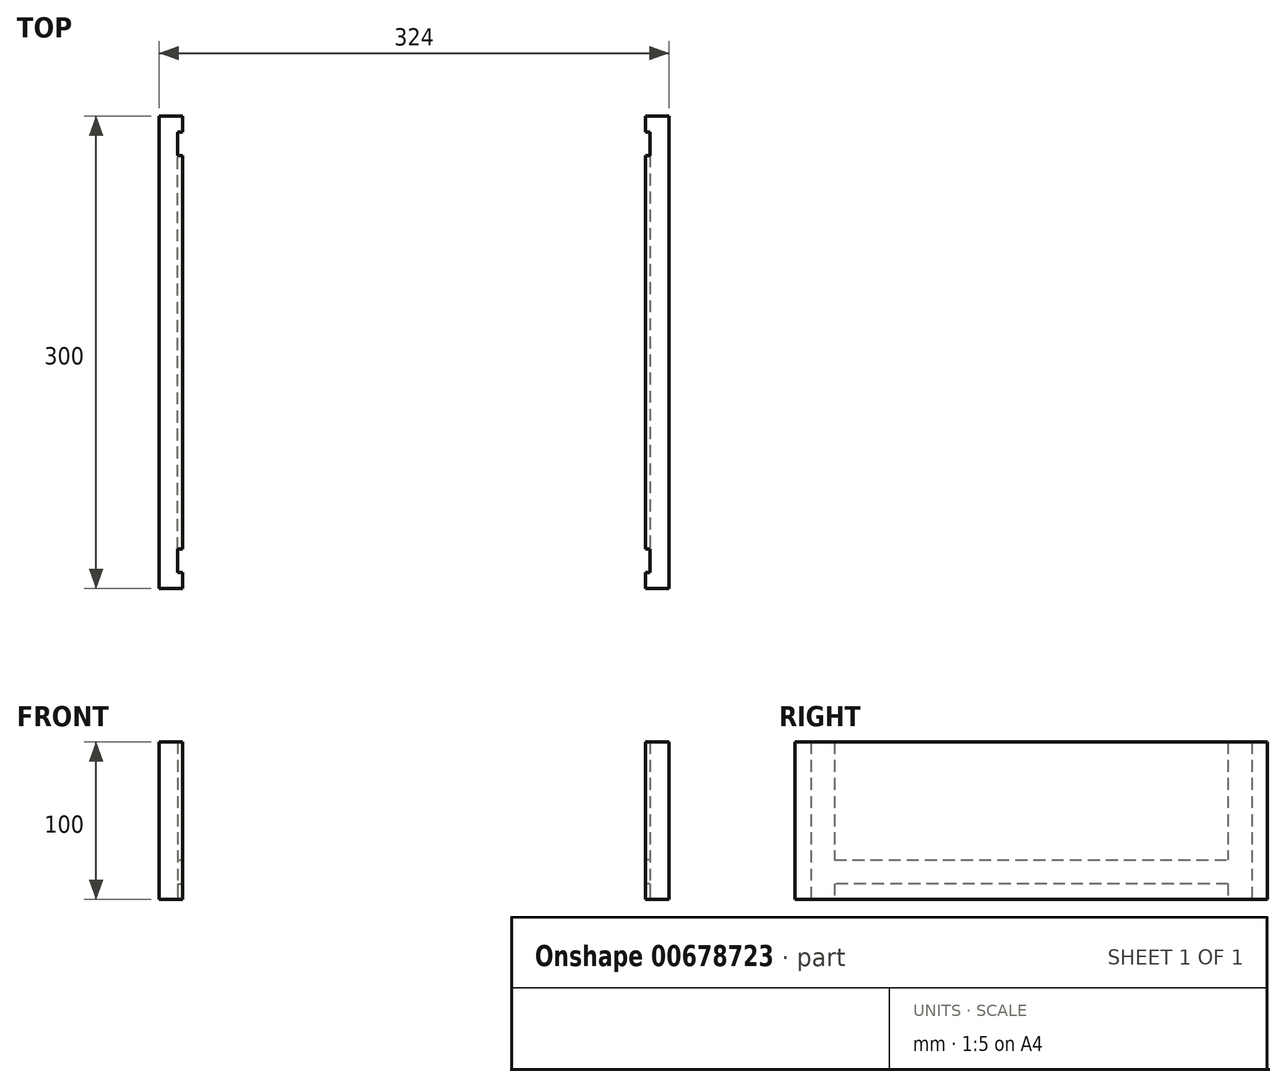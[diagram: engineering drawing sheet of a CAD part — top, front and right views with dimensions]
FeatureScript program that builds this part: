
annotation { "Feature Type Name" : "Feature", "Feature Type Description" : "" }
export const myFeature = defineFeature(function(context is Context, id is Id, definition is map)
    precondition{}
    {
        {
            var Q0;
            Q0=qCreatedBy(makeId("Top.planeOp"),FACE);
            var sketch = newSketch(context, id + "F0", { "sketchPlane" : qUnion([Q0])});
            skLineSegment(sketch, "E0", {"start": v(-162, 0) * mm, "end": v(-147, 0) * mm});
            skLineSegment(sketch, "E1", {"start": v(-147, 0) * mm, "end": v(-147, 10) * mm});
            skLineSegment(sketch, "E2", {"start": v(-147, 10) * mm, "end": v(-150, 10) * mm});
            skLineSegment(sketch, "E3", {"start": v(-150, 10) * mm, "end": v(-150, 25) * mm});
            skLineSegment(sketch, "E4", {"start": v(-150, 25) * mm, "end": v(-147, 25) * mm});
            skLineSegment(sketch, "E5", {"start": v(-147, 25) * mm, "end": v(-147, 275) * mm});
            skLineSegment(sketch, "E6", {"start": v(-147, 275) * mm, "end": v(-150, 275) * mm});
            skLineSegment(sketch, "E7", {"start": v(-150, 275) * mm, "end": v(-150, 290) * mm});
            skLineSegment(sketch, "E8", {"start": v(-150, 290) * mm, "end": v(-147, 290) * mm});
            skLineSegment(sketch, "E9", {"start": v(-147, 290) * mm, "end": v(-147, 300) * mm});
            skLineSegment(sketch, "E10", {"start": v(-147, 300) * mm, "end": v(-162, 300) * mm});
            skLineSegment(sketch, "E11", {"start": v(-162, 300) * mm, "end": v(-162, 0) * mm});
            skLineSegment(sketch, "E12", {"start": v(0, 0) * mm, "end": v(0, 300) * mm, "construction": true});
            skLineSegment(sketch, "E13", {"start": v(-147, 300) * mm, "end": v(0, 300) * mm, "construction": true});
            skSolve(sketch);
        }
        {
            var Q0;
            Q0 = qSketchRegion(id + "F0", true);
            extrude(context, id + "F1", {"entities" : qUnion([Q0]), "depth" : 100 * mm, "offsetDistance" : 25 * mm});
        }
        {
            var Q0;
            Q0=makeQuery(id+"F1.opExtrude","SWEPT_FACE",FACE,{"disambiguationData":[OSD([sQuery(id+"F0.wireOp",EDGE,"E5")])]});
            var sketch = newSketch(context, id + "F2", { "sketchPlane" : qUnion([Q0])});
            skLineSegment(sketch, "E14", {"start": v(275, 10) * mm, "end": v(25, 10) * mm});
            skLineSegment(sketch, "E15", {"start": v(25, 10) * mm, "end": v(25, 25) * mm});
            skLineSegment(sketch, "E16", {"start": v(25, 25) * mm, "end": v(275, 25) * mm});
            skLineSegment(sketch, "E17", {"start": v(275, 25) * mm, "end": v(275, 10) * mm});
            skSolve(sketch);
        }
        {
            var Q0;
            Q0 = qSketchRegion(id + "F2", true);
            var Q1;
            Q1=makeQuery(id+"F1.opExtrude","SWEPT_FACE",FACE,{"disambiguationData":[OSD([sQuery(id+"F0.wireOp",EDGE,"E3")])]});
            extrude(context, id + "F3", {"entities" : qUnion([Q0]), "operationType" : NewBodyOperationType.REMOVE, "endBound" : BoundingType.UP_TO_SURFACE, "oppositeDirection" : true, "depth" : 5 * mm, "endBoundEntityFace" : qUnion([Q1]), "offsetDistance" : 25 * mm});
        }
        {
            var Q0;
            Q0=makeQuery(id+"F1.opExtrude","SWEPT_BODY",BODY,{"disambiguationData":[OSD([sQuery(id+"F0.wireOp",EDGE,"E0"),sQuery(id+"F0.wireOp",EDGE,"E1"),sQuery(id+"F0.wireOp",EDGE,"E2"),sQuery(id+"F0.wireOp",EDGE,"E3"),sQuery(id+"F0.wireOp",EDGE,"E4"),sQuery(id+"F0.wireOp",EDGE,"E5"),sQuery(id+"F0.wireOp",EDGE,"E6"),sQuery(id+"F0.wireOp",EDGE,"E7"),sQuery(id+"F0.wireOp",EDGE,"E8"),sQuery(id+"F0.wireOp",EDGE,"E9"),sQuery(id+"F0.wireOp",EDGE,"E10"),sQuery(id+"F0.wireOp",EDGE,"E11")])]});
            var Q1;
            Q1=qCreatedBy(makeId("Right.planeOp"),FACE);
            mirror(context, id + "F4", {"entities" : qUnion([Q0]), "mirrorPlane" : qUnion([Q1])});
        }
    });
